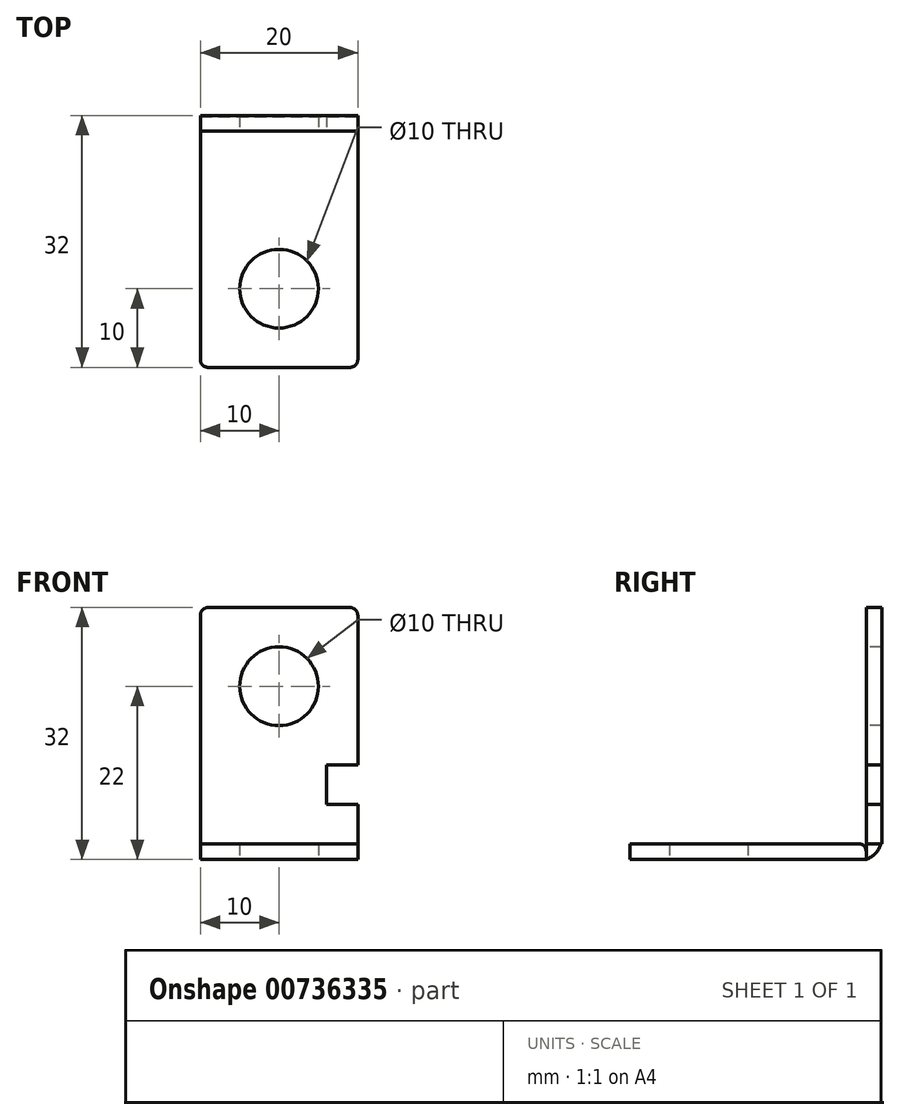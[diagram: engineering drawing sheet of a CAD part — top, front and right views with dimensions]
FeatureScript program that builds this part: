
annotation { "Feature Type Name" : "Feature", "Feature Type Description" : "" }
export const myFeature = defineFeature(function(context is Context, id is Id, definition is map)
    precondition{}
    {
        {
            var Q0;
            Q0=qCreatedBy(makeId("Top.planeOp"),FACE);
            var sketch = newSketch(context, id + "F0", { "sketchPlane" : qUnion([Q0])});
            skLineSegment(sketch, "E0.bottom", {"start": v(0, 0) * mm, "end": v(20, 0) * mm});
            skLineSegment(sketch, "E0.top", {"start": v(0, 30) * mm, "end": v(20, 30) * mm});
            skLineSegment(sketch, "E0.left", {"start": v(0, 0) * mm, "end": v(0, 30) * mm});
            skLineSegment(sketch, "E0.right", {"start": v(20, 0) * mm, "end": v(20, 30) * mm});
            skCircle(sketch, "E1", {"center": v(10, 10) * mm, "radius": 5 * mm});
            skSolve(sketch);
        }
        {
            var Q0;
            Q0 = qSketchRegion(id + "F0", true);
            extrude(context, id + "F1", {"entities" : qUnion([Q0]), "depth" : 2 * mm, "offsetDistance" : 25 * mm});
        }
        {
            var Q0;
            Q0=makeQuery(id+"F1.opExtrude","SWEPT_FACE",FACE,{"disambiguationData":[OSD([sQuery(id+"F0.wireOp",EDGE,"E0.top")])]});
            var sketch = newSketch(context, id + "F2", { "sketchPlane" : qUnion([Q0])});
            skLineSegment(sketch, "E2.bottom", {"start": v(-20, 2) * mm, "end": v(0, 2) * mm});
            skLineSegment(sketch, "E2.top", {"start": v(-20, 32) * mm, "end": v(0, 32) * mm});
            skLineSegment(sketch, "E2.left", {"start": v(-20, 2) * mm, "end": v(-20, 32) * mm});
            skLineSegment(sketch, "E2.right", {"start": v(0, 2) * mm, "end": v(0, 32) * mm});
            skLineSegment(sketch, "E3.bottom", {"start": v(-20, 12) * mm, "end": v(-16, 12) * mm});
            skLineSegment(sketch, "E3.top", {"start": v(-20, 7) * mm, "end": v(-16, 7) * mm});
            skLineSegment(sketch, "E3.left", {"start": v(-20, 12) * mm, "end": v(-20, 7) * mm});
            skLineSegment(sketch, "E3.right", {"start": v(-16, 12) * mm, "end": v(-16, 7) * mm});
            skCircle(sketch, "E4", {"center": v(-10, 22) * mm, "radius": 5 * mm});
            skSolve(sketch);
        }
        {
            var Q0;
            {var subQ4=sQuery(id+"F2.wireOp",EDGE,"E2.bottom");Q0=makeQuery(id+"F2.imprint","IMPRINT",FACE,{"disambiguationData":[TD([[makeQuery(id+"F2.imprint","IMPRINT",EDGE,{"derivedFrom":subQ4}),-1.0]])]});}
            extrude(context, id + "F3", {"entities" : qUnion([Q0]), "depth" : 2 * mm, "offsetDistance" : 25 * mm});
        }
        {
            var Q0;
            Q0=makeQuery(id+"F1.opExtrude","SWEPT_FACE",FACE,{"disambiguationData":[OSD([sQuery(id+"F0.wireOp",EDGE,"E0.top")])]});
            var sketch = newSketch(context, id + "F4", { "sketchPlane" : qUnion([Q0])});
            skLineSegment(sketch, "E5.bottom", {"start": v(-20, 0) * mm, "end": v(0, 0) * mm});
            skLineSegment(sketch, "E5.top", {"start": v(-20, 2) * mm, "end": v(0, 2) * mm});
            skLineSegment(sketch, "E5.left", {"start": v(-20, 0) * mm, "end": v(-20, 2) * mm});
            skLineSegment(sketch, "E5.right", {"start": v(0, 0) * mm, "end": v(0, 2) * mm});
            skSolve(sketch);
        }
        {
            var Q0;
            Q0 = qSketchRegion(id + "F4", true);
            extrude(context, id + "F5", {"entities" : qUnion([Q0]), "depth" : 2 * mm, "offsetDistance" : 25 * mm});
        }
        {
            var Q0;
            Q0=makeQuery(id+"F1.opExtrude","SWEPT_EDGE",EDGE,{"disambiguationData":[OSD([sQuery(id+"F0.wireOp",EDGE,"E0.bottom"),sQuery(id+"F0.wireOp",EDGE,"E0.right")])]});
            var Q1;
            Q1=makeQuery(id+"F1.opExtrude","SWEPT_EDGE",EDGE,{"disambiguationData":[OSD([sQuery(id+"F0.wireOp",EDGE,"E0.bottom"),sQuery(id+"F0.wireOp",EDGE,"E0.left")])]});
            var Q2;
            Q2=makeQuery(id+"F3.opExtrude","SWEPT_EDGE",EDGE,{"disambiguationData":[OSD([sQuery(id+"F2.wireOp",EDGE,"E2.top"),sQuery(id+"F2.wireOp",EDGE,"E2.left")])]});
            var Q3;
            Q3=makeQuery(id+"F3.opExtrude","SWEPT_EDGE",EDGE,{"disambiguationData":[OSD([sQuery(id+"F2.wireOp",EDGE,"E2.top"),sQuery(id+"F2.wireOp",EDGE,"E2.right")])]});
            fillet(context, id + "F6", {"entities" : qUnion([Q0, Q1, Q2, Q3]), "radius" : 1 * mm, "tangentPropagation" : true, "allowEdgeOverflow" : false});
        }
        {
            var Q0;
            Q0=makeQuery(id+"F1.opExtrude","CAP_EDGE",EDGE,{"disambiguationData":[OSD([sQuery(id+"F0.wireOp",EDGE,"E0.top")])],"isStart":false});
            fillet(context, id + "F7", {"entities" : qUnion([Q0]), "radius" : 1 * mm, "tangentPropagation" : true, "allowEdgeOverflow" : false});
        }
        {
            var Q0;
            Q0=makeQuery(id+"F5.opExtrude","CAP_EDGE",EDGE,{"disambiguationData":[OSD([sQuery(id+"F4.wireOp",EDGE,"E5.bottom")])],"isStart":false});
            fillet(context, id + "F8", {"entities" : qUnion([Q0]), "radius" : 3 * mm, "tangentPropagation" : true, "allowEdgeOverflow" : false});
        }
    });
